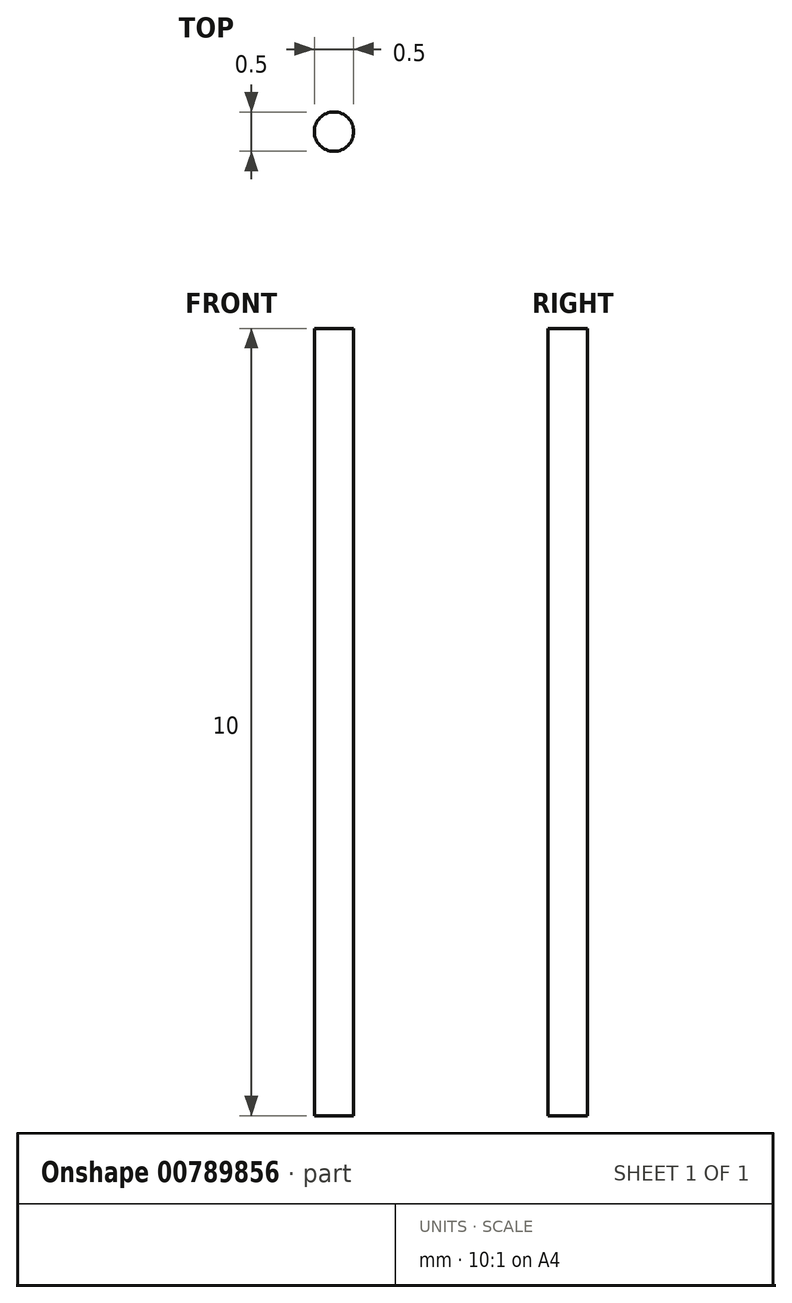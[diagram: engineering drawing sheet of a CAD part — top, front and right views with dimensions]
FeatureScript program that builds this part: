
annotation { "Feature Type Name" : "Feature", "Feature Type Description" : "" }
export const myFeature = defineFeature(function(context is Context, id is Id, definition is map)
    precondition{}
    {
        {
            var Q0;
            Q0=qCreatedBy(makeId("Top.planeOp"),FACE);
            var sketch = newSketch(context, id + "F0", { "sketchPlane" : qUnion([Q0])});
            skCircle(sketch, "E0", {"center": v(0, 0) * mm, "radius": 0.25 * mm});
            skSolve(sketch);
        }
        {
            var Q0;
            Q0 = qSketchRegion(id + "F0", true);
            extrude(context, id + "F1", {"entities" : qUnion([Q0]), "depth" : 10 * mm, "offsetDistance" : 25 * mm});
        }
    });
